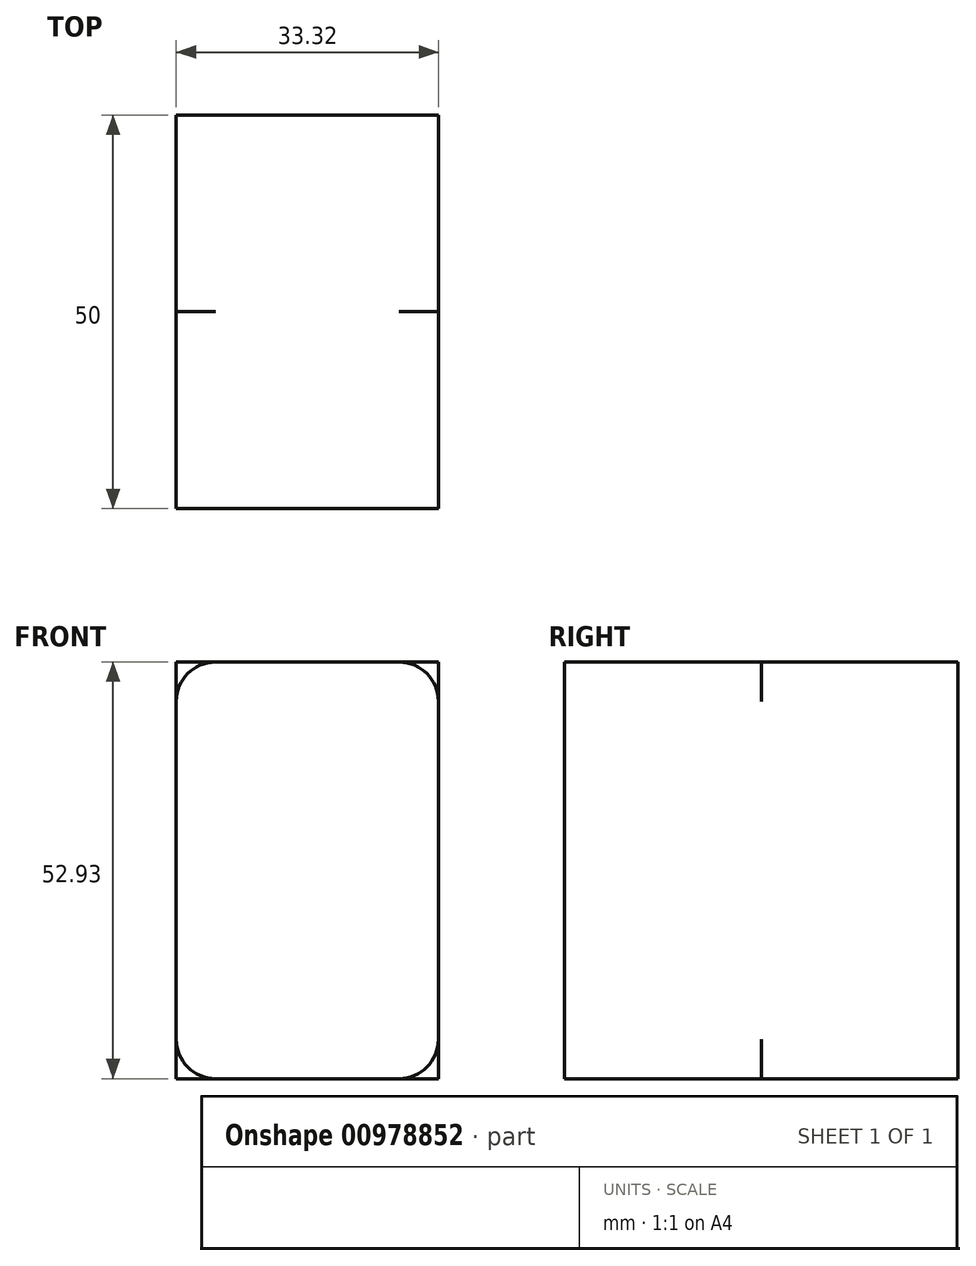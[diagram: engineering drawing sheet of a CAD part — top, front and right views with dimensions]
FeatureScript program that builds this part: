
annotation { "Feature Type Name" : "Feature", "Feature Type Description" : "" }
export const myFeature = defineFeature(function(context is Context, id is Id, definition is map)
    precondition{}
    {
        {
            var Q0;
            Q0=qCreatedBy(makeId("Front.planeOp"),FACE);
            var sketch = newSketch(context, id + "F0", { "sketchPlane" : qUnion([Q0])});
            skLineSegment(sketch, "E0.bottom", {"start": v(-110.32, 27.92) * mm, "end": v(-77, 27.92) * mm});
            skLineSegment(sketch, "E0.top", {"start": v(-110.32, -25) * mm, "end": v(-77, -25) * mm});
            skLineSegment(sketch, "E0.left", {"start": v(-110.32, 27.92) * mm, "end": v(-110.32, -25) * mm});
            skLineSegment(sketch, "E0.right", {"start": v(-77, 27.92) * mm, "end": v(-77, -25) * mm});
            skSolve(sketch);
        }
        {
            var Q0;
            Q0=sQuery(id+"F0.wireOp",EDGE,"E0.bottom");
            var Q1;
            Q1=sQuery(id+"F0.wireOp",EDGE,"E0.right");
            var Q2;
            Q2=sQuery(id+"F0.wireOp",EDGE,"E0.top");
            var Q3;
            Q3=sQuery(id+"F0.wireOp",EDGE,"E0.left");
            extrude(context, id + "F1", {"bodyType" : ToolBodyType.SURFACE, "surfaceEntities" : qUnion([Q0, Q1, Q2, Q3]), "depth" : 25 * mm, "offsetDistance" : 25 * mm});
        }
        {
            var Q0;
            Q0=makeQuery(id+"F1.opExtrude","SWEPT_FACE",FACE,{"disambiguationData":[OSD([sQuery(id+"F0.wireOp",EDGE,"E0.bottom")])]});
            var Q1;
            Q1=makeQuery(id+"F1.opExtrude","SWEPT_FACE",FACE,{"disambiguationData":[OSD([sQuery(id+"F0.wireOp",EDGE,"E0.top")])]});
            fillet(context, id + "F2", {"entities" : qUnion([Q0, Q1]), "radius" : 5 * mm, "tangentPropagation" : true, "allowEdgeOverflow" : false});
        }
        {
            var Q0;
            Q0=sQuery(id+"F0.wireOp",EDGE,"E0.bottom");
            var Q1;
            Q1=sQuery(id+"F0.wireOp",EDGE,"E0.right");
            var Q2;
            Q2=sQuery(id+"F0.wireOp",EDGE,"E0.top");
            var Q3;
            Q3=sQuery(id+"F0.wireOp",EDGE,"E0.left");
            extrude(context, id + "F3", {"bodyType" : ToolBodyType.SURFACE, "surfaceOperationType" : NewSurfaceOperationType.ADD, "surfaceEntities" : qUnion([Q0, Q1, Q2, Q3]), "oppositeDirection" : true, "depth" : 25 * mm, "offsetDistance" : 25 * mm});
        }
    });
